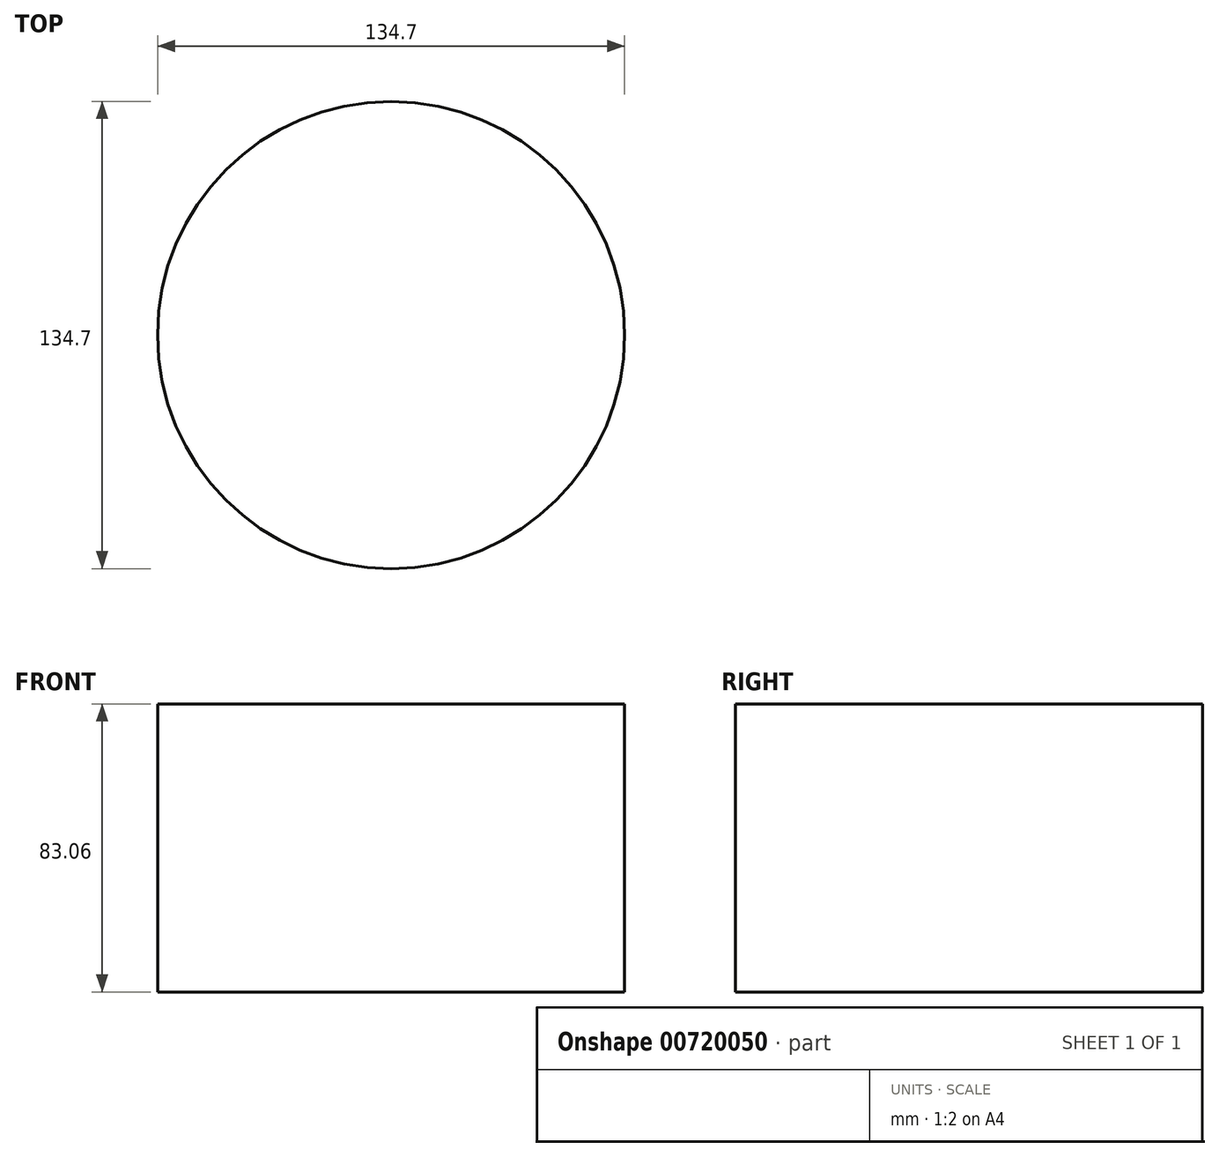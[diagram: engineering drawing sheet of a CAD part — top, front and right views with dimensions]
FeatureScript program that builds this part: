
annotation { "Feature Type Name" : "Feature", "Feature Type Description" : "" }
export const myFeature = defineFeature(function(context is Context, id is Id, definition is map)
    precondition{}
    {
        {
            var Q0;
            Q0=qCreatedBy(makeId("Top.planeOp"),FACE);
            var sketch = newSketch(context, id + "F0", { "sketchPlane" : qUnion([Q0])});
            skCircle(sketch, "E0", {"center": v(0, 0) * mm, "radius": 67.35 * mm});
            skSolve(sketch);
        }
        {
            var Q0;
            Q0=makeQuery(id+"F0.imprint","IMPRINT",FACE,{"disambiguationData":[TD([[makeQuery(id+"F0.imprint","IMPRINT",EDGE,{"derivedFrom":sQuery(id+"F0.wireOp",EDGE,"E0")}),1.0]])]});
            extrude(context, id + "F1", {"entities" : qUnion([Q0]), "depth" : 83.06 * mm, "offsetDistance" : 25.4 * mm});
        }
    });
